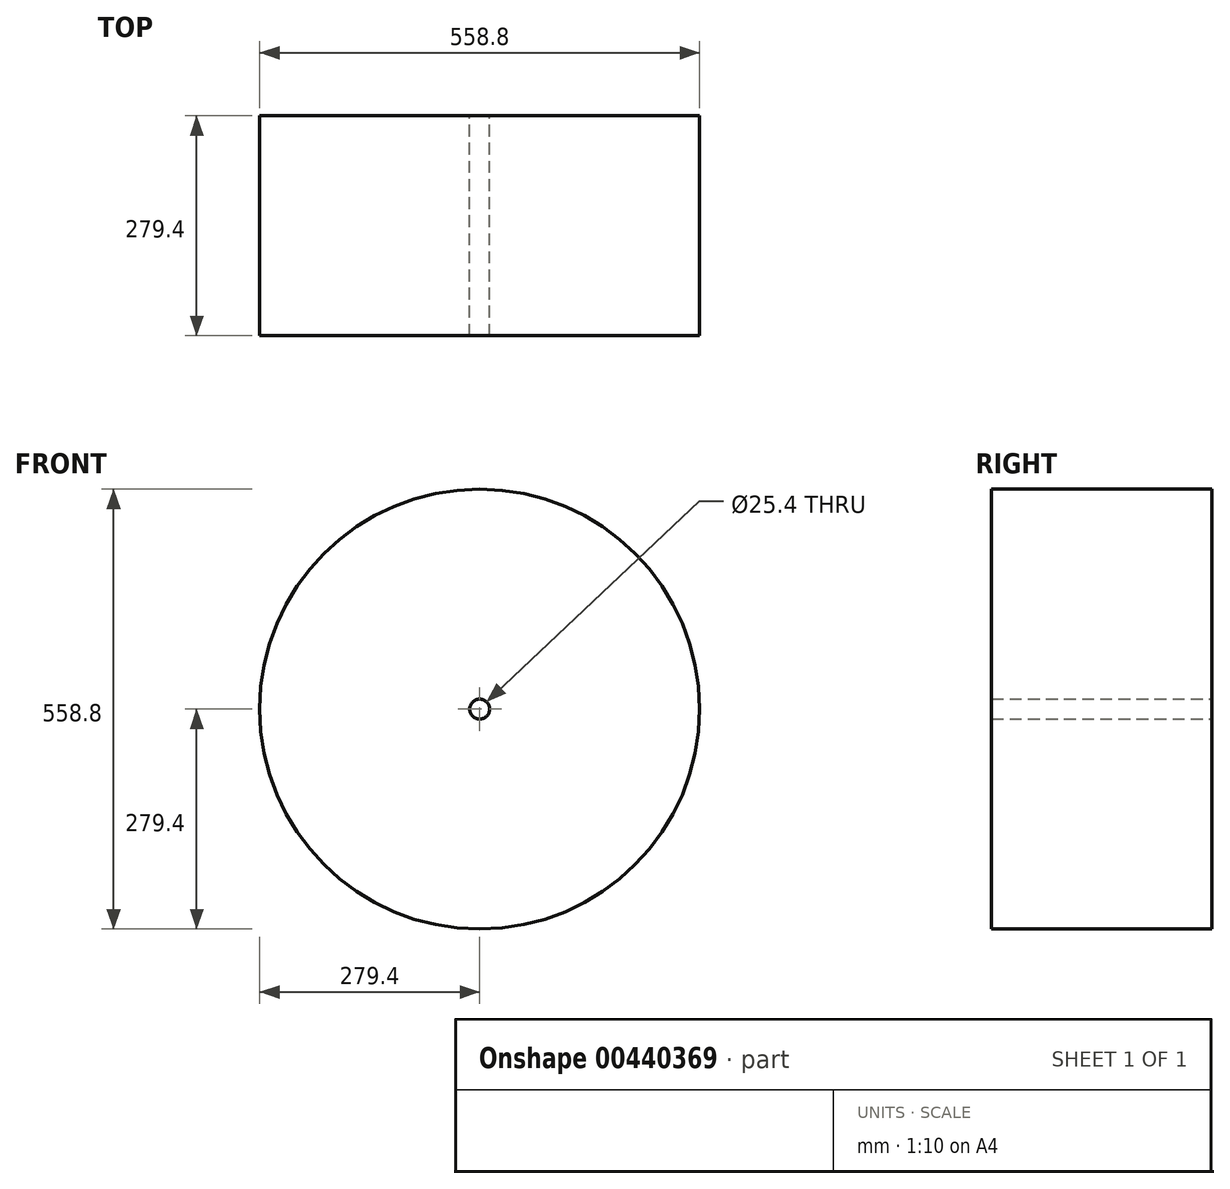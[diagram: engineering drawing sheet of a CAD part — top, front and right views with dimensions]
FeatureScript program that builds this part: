
annotation { "Feature Type Name" : "Feature", "Feature Type Description" : "" }
export const myFeature = defineFeature(function(context is Context, id is Id, definition is map)
    precondition{}
    {
        {
            var Q0;
            Q0=qCreatedBy(makeId("Front.planeOp"),FACE);
            var sketch = newSketch(context, id + "F0", { "sketchPlane" : qUnion([Q0])});
            skCircle(sketch, "E0", {"center": v(0, 0) * mm, "radius": 279.4 * mm});
            skCircle(sketch, "E1", {"center": v(0, 0) * mm, "radius": 12.7 * mm});
            skSolve(sketch);
        }
        {
            var Q0;
            Q0=makeQuery(id+"F0.imprint","IMPRINT",FACE,{"disambiguationData":[TD([[makeQuery(id+"F0.imprint","IMPRINT",EDGE,{"derivedFrom":sQuery(id+"F0.wireOp",EDGE,"E0")}),1.0]])]});
            extrude(context, id + "F1", {"entities" : qUnion([Q0]), "endBound" : BoundingType.SYMMETRIC, "depth" : 279.4 * mm});
        }
    });
